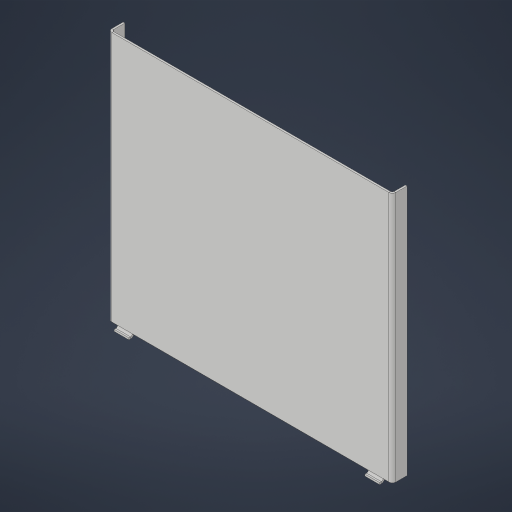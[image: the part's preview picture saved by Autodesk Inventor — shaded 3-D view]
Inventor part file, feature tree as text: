
AUTODESK INVENTOR PART (.ipt)
format: ipt  version: 2023.4 (Build 274418000, 418)  size: 222,208 bytes
history: native  units: in
note: dims shown in document units (in); Inventor stores cm internally (conversion verified against a paired STEP export)
features: sheet_metal_op x7, sketch x3, other x3, projected_geometry x1
ambient origin geometry x8: Origin, YZ Plane, XZ Plane, XY Plane, X Axis, Y Axis, Z Axis, Center Point
bodies: Solid1 (feature_tree)
feature tree (14):
  sheet_metal_op  "Face1"
  sheet_metal_op  "Flange1"
  sketch  "Sketch3"  dims[d2=0.12in d3=0.12in d4=0.06in d5=0.24in d6=0.12in d7=1.0in d8=90.0deg d9=0.12in d10=0.48in d11=0.12in d12=0.12in d13=0.375in d14=1.0in d15=8.0in d16=8.0in d17=1.0in d18=0.12in d19=0.12in d20=0.06in d21=0.24in d22=0.12in d23=0.25in d24=0.12in d25=0.06in d26=0.24in d27=0.12in d28=90.0deg d29=0.12in]
  sheet_metal_op  "Face2"
  sheet_metal_op  "Fold1"
  sketch  "Sketch1"  dims[d0=19.25in]
  other  "Plate1"
  sketch  "Sketch2"  dims[d1=17.0in]
  other  "Plate2"
  sheet_metal_op  "Bend1"
  sheet_metal_op  "Corner1"
  other  "Plate3"
  sheet_metal_op  "Bend2"
  projected_geometry  "Project Cut Edges1"
